# Revit family: Rohrschelle Maxima PSM, M16, Ø132-273, o.D
name_source: partatom
category: HLS-Bauteile
revit_build: Autodesk Revit 2017 (Build: 20190507_1515(x64)
units: mm (PartAtom-declared; Revit-internal decimal feet)

## family parameters
Arbeitsebenenbasiert = Nein
Beim Laden mit Abzugskörper schneiden = Nein
Bemaßung runder Anschluss = Durchmesser verwenden
Gemeinsam genutzt = Ja
Immer vertikal = Nein
Raumberechnungspunkt = Nein
Teiletyp = Normal

## types (11) — shared parameters
A = 14 mm  [stored 0.0459318 ft]
Anschluss = M16
Anschlußhöhe = 24 mm
Bauart = zweiteilig
Brandschutz = RAL-GZ 656
DF1 = 30 mm  [stored 0.0984252 ft]
DF2 = 35 mm  [stored 0.114829 ft]
DVS = 20 mm  [stored 0.0656168 ft]
Fabrikat = MEFA
Firma = MEFA Befestigungs- und Montagesysteme GmbH
HGA = 10 mm  [stored 0.0328084 ft]
Kurztext1 = Rohrschelle Maxima PSM 35x4,0
MB = 35 mm  [stored 0.114829 ft]
MD = 4 mm  [stored 0.0131234 ft]
Material = Stahl
Materialmaße = 35x4,0 mm
Materialname = S235
Mengeneinheit = St
Oberflaeche = galvanisch verzinkt
Verschluss = Pendelsteckmuttern
Verschluss-Schraube = M10
max. zul. Last = 6.30 kN
max. zul. Last horizontal = 0.00 kN
max. zul. Last vertikal = 0.00 kN
vpe = 1 St
zero-valued in all types: Nennweite DN Rohr, Rohraußendurchmesser, Stärke Material

## per-type parameters (varying)
| type | AB | Achsabstand | Artikelnummer | B | Breite | D | Dmax | Dmin | EAN | Gewicht | Gewicht pro Bauteil | H | Kurztext2 | R | RM | Rohraußendurchmesser Zoll | S | max. Höhe | max. Rohraußendurchmesser | min. Rohraußendurchmesser |
| Maxima PSM, M16, Ø132-137, o.D. | 5 mm  [stored 0.0164042 ft] | 180 mm | 0081654 | 210 mm | 210 mm | 137 mm  [stored 0.449475 ft] | 137 mm  [stored 0.449475 ft] | 132 mm  [stored 0.433071 ft] | 4250928406071 | 0.73 kg | 0.73 kg | 155 mm  [stored 0.50853 ft] | 132 - 137 mm M16 | 69 mm | 73 mm | Zoll | 180 mm | 165 mm | 137 mm  [stored 0.449475 ft] | 132 mm  [stored 0.433071 ft] |
| Maxima PSM, M16, Ø139-144, o.D. | 5 mm  [stored 0.0164042 ft] | 187 mm | 0081657 | 217 mm | 217 mm | 144 mm  [stored 0.472441 ft] | 144 mm  [stored 0.472441 ft] | 139 mm  [stored 0.456037 ft] | 4250928406095 | 0.75 kg | 0.75 kg | 162 mm  [stored 0.531496 ft] | 139 - 144 mm M16 | 72 mm  [stored 0.23622 ft] | 76 mm  [stored 0.249344 ft] | 5 Zoll | 187 mm | 172 mm | 144 mm  [stored 0.472441 ft] | 139 mm  [stored 0.456037 ft] |
| Maxima PSM, M16, Ø149-154, o.D. | 5 mm  [stored 0.0164042 ft] | 197 mm | 0081667 | 227 mm | 227 mm | 154 mm  [stored 0.505249 ft] | 154 mm  [stored 0.505249 ft] | 149 mm  [stored 0.488845 ft] | 4250928406118 | 0.79 kg | 0.79 kg | 172 mm | 149 - 154 mm M16 | 77 mm  [stored 0.252625 ft] | 81 mm  [stored 0.265748 ft] | Zoll | 197 mm | 182 mm | 154 mm  [stored 0.505249 ft] | 149 mm  [stored 0.488845 ft] |
| Maxima PSM, M16, Ø157-162, o.D. | 5 mm  [stored 0.0164042 ft] | 205 mm | 0081675 | 235 mm | 235 mm | 162 mm  [stored 0.531496 ft] | 162 mm  [stored 0.531496 ft] | 157 mm  [stored 0.515092 ft] | 4250928406156 | 0.81 kg | 0.81 kg | 180 mm | 157 - 162 mm M16 | 81 mm  [stored 0.265748 ft] | 85 mm  [stored 0.278871 ft] | Zoll | 205 mm | 190 mm | 162 mm  [stored 0.531496 ft] | 157 mm  [stored 0.515092 ft] |
| Maxima PSM, M16, Ø164-168, o.D. | 4 mm  [stored 0.0131234 ft] | 211 mm | 0081704 | 241 mm | 241 mm | 168 mm | 168 mm | 164 mm  [stored 0.538058 ft] | 4250928406170 | 0.84 kg | 0.84 kg | 186 mm | 164 - 168 mm M16 | 84 mm  [stored 0.275591 ft] | 88 mm | 6 Zoll | 211 mm | 196 mm | 168 mm | 164 mm  [stored 0.538058 ft] |
| Maxima PSM, M16, Ø189-193, o.D. | 4 mm  [stored 0.0131234 ft] | 236 mm | 0081739 | 266 mm | 266 mm | 193 mm | 193 mm | 189 mm | 4250928406194 | 0.93 kg | 0.93 kg | 211 mm | 189 - 193 mm M16 | 97 mm | 101 mm | Zoll | 236 mm | 221 mm | 193 mm | 189 mm |
| Maxima PSM, M16, Ø195-200, o.D. | 5 mm  [stored 0.0164042 ft] | 243 mm | 0081746 | 273 mm | 273 mm | 200 mm | 200 mm | 195 mm | 4250928406200 | 0.95 kg | 0.95 kg | 218 mm | 195 - 200 mm M16 | 100 mm  [stored 0.328084 ft] | 104 mm | Zoll | 243 mm | 228 mm | 200 mm | 195 mm |
| Maxima PSM, M16, Ø210-215, o.D. | 5 mm  [stored 0.0164042 ft] | 258 mm | 0081762 | 288 mm | 288 mm | 215 mm | 215 mm | 210 mm | 4250928406231 | 1.00 kg | 1.00 kg | 233 mm | 210 - 215 mm M16 | 108 mm | 112 mm | Zoll | 258 mm | 243 mm | 215 mm | 210 mm |
| Maxima PSM, M16, Ø219-225, o.D. | 6 mm  [stored 0.019685 ft] | 268 mm | 0081790 | 298 mm | 298 mm | 225 mm | 225 mm | 219 mm | 4250928406255 | 1.04 kg | 1.04 kg | 243 mm | 219 - 225 mm M16 | 113 mm | 117 mm | 8 Zoll | 268 mm | 253 mm | 225 mm | 219 mm |
| Maxima PSM, M16, Ø244-250, o.D. | 6 mm  [stored 0.019685 ft] | 293 mm | 0081818 | 323 mm | 323 mm | 250 mm | 250 mm | 244 mm | 4250928406286 | 1.13 kg | 1.13 kg | 268 mm | 244 - 250 mm M16 | 125 mm  [stored 0.410105 ft] | 129 mm | Zoll | 293 mm | 280 mm | 250 mm | 244 mm |
| Maxima PSM, M16, Ø269-273, o.D. | 4 mm  [stored 0.0131234 ft] | 316 mm | 0081843 | 346 mm | 346 mm | 273 mm | 273 mm | 269 mm | 4250928406309 | 1.21 kg | 1.21 kg | 291 mm | 269 - 273 mm M16 | 137 mm  [stored 0.449475 ft] | 141 mm | 10 Zoll | 316 mm | 301 mm | 273 mm | 269 mm |

note: [stored X ft] marks values corroborated as IEEE doubles in the binary element streams (Revit-internal decimal feet)

## geometry (parser evidence)
native form markers: Sweep x2
no freeform markers — native parametric forms only
